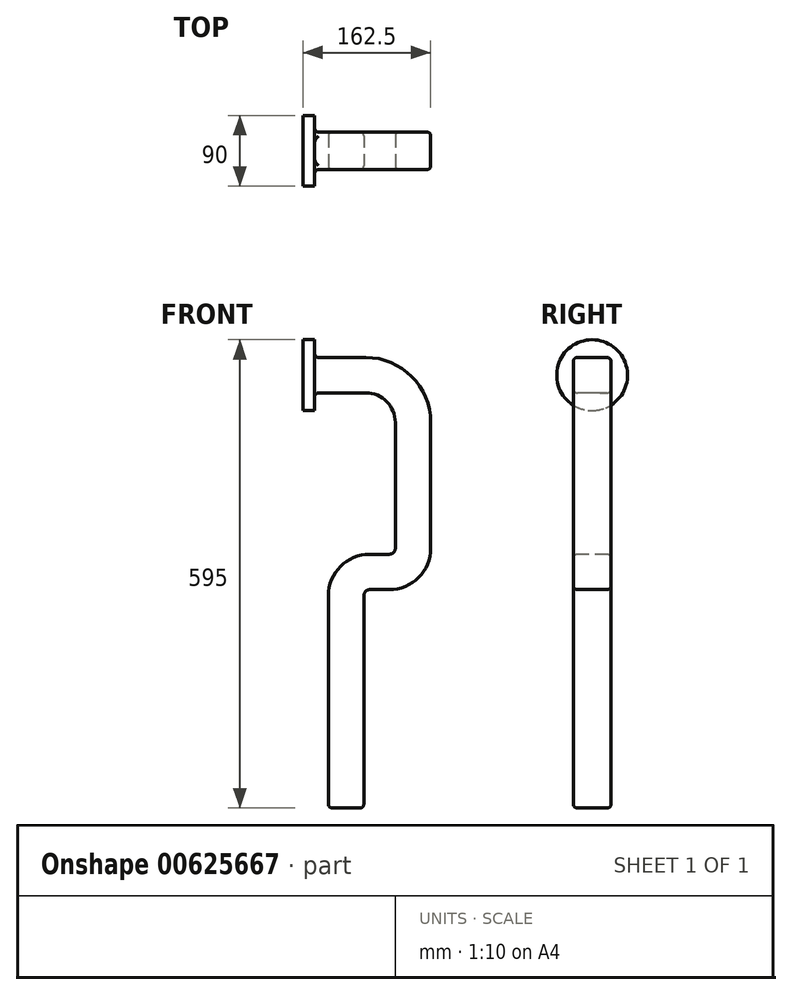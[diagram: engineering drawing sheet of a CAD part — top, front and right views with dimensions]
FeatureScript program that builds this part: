
annotation { "Feature Type Name" : "Feature", "Feature Type Description" : "" }
export const myFeature = defineFeature(function(context is Context, id is Id, definition is map)
    precondition{}
    {
        {
            var Q0;
            Q0=qCreatedBy(makeId("Right.planeOp"),FACE);
            var sketch = newSketch(context, id + "F0", { "sketchPlane" : qUnion([Q0])});
            skCircle(sketch, "E0", {"center": v(0, 0) * mm, "radius": 45 * mm});
            skSolve(sketch);
        }
        {
            var Q0;
            Q0=makeQuery(id+"F0.imprint","IMPRINT",FACE,{"disambiguationData":[TD([[makeQuery(id+"F0.imprint","IMPRINT",EDGE,{"derivedFrom":sQuery(id+"F0.wireOp",EDGE,"E0")}),1.0]])]});
            var Q1;
            Q1=sQuery(id+"F0.wireOp",EDGE,"E0");
            extrude(context, id + "F1", {"entities" : qUnion([Q0]), "surfaceEntities" : qUnion([Q1]), "depth" : 15 * mm, "offsetDistance" : 25 * mm});
        }
        {
            var Q0;
            Q0=makeQuery(id+"F1.opExtrude","CAP_FACE",FACE,{"disambiguationData":[OSD([sQuery(id+"F0.wireOp",EDGE,"E0")])],"isStart":false});
            var sketch = newSketch(context, id + "F2", { "sketchPlane" : qUnion([Q0])});
            skLineSegment(sketch, "E1.bottom", {"start": v(23.85, -22.5) * mm, "end": v(-23.85, -22.5) * mm});
            skLineSegment(sketch, "E1.top", {"start": v(23.85, 22.5) * mm, "end": v(-23.85, 22.5) * mm});
            skLineSegment(sketch, "E1.left", {"start": v(23.85, -22.5) * mm, "end": v(23.85, 22.5) * mm});
            skLineSegment(sketch, "E1.right", {"start": v(-23.85, -22.5) * mm, "end": v(-23.85, 22.5) * mm});
            skPoint(sketch, "E1.middle", {"position": v(0, 0) * mm});
            skSolve(sketch);
        }
        {
            var Q0;
            Q0=qCreatedBy(makeId("Front.planeOp"),FACE);
            var sketch = newSketch(context, id + "F3", { "sketchPlane" : qUnion([Q0])});
            skLineSegment(sketch, "E2", {"start": v(15, 0) * mm, "end": v(80, 0) * mm});
            skLineSegment(sketch, "E3", {"start": v(140, -60) * mm, "end": v(140, -220) * mm});
            skLineSegment(sketch, "E4", {"start": v(110, -250) * mm, "end": v(85, -250) * mm});
            skLineSegment(sketch, "E5", {"start": v(55, -280) * mm, "end": v(55, -550) * mm});
            skPoint(sketch, "E6.visualSharp", {"position": v(140, 0) * mm});
            skArc(sketch, "E6.filletArc", {"start": v(140, -60) * mm, "mid": v(122.43, -17.57) * mm, "end": v(80, 0) * mm});
            skPoint(sketch, "E7.visualSharp", {"position": v(140, -250) * mm});
            skArc(sketch, "E7.filletArc", {"start": v(110, -250) * mm, "mid": v(131.21, -241.21) * mm, "end": v(140, -220) * mm});
            skPoint(sketch, "E8.visualSharp", {"position": v(55, -250) * mm});
            skArc(sketch, "E8.filletArc", {"start": v(85, -250) * mm, "mid": v(63.79, -258.79) * mm, "end": v(55, -280) * mm});
            skSolve(sketch);
        }
        {
            var Q0;
            Q0=makeQuery(id+"F2.imprint","IMPRINT",FACE,{"disambiguationData":[TD([[makeQuery(id+"F2.imprint","IMPRINT",EDGE,{"derivedFrom":sQuery(id+"F2.wireOp",EDGE,"E1.bottom")}),-1.0]])]});
            var Q1;
            Q1=sQuery(id+"F3.wireOp",EDGE,"E2");
            var Q2;
            Q2=sQuery(id+"F3.wireOp",EDGE,"E6.filletArc");
            var Q3;
            Q3=sQuery(id+"F3.wireOp",EDGE,"E3");
            var Q4;
            Q4=sQuery(id+"F3.wireOp",EDGE,"E7.filletArc");
            var Q5;
            Q5=sQuery(id+"F3.wireOp",EDGE,"E4");
            var Q6;
            Q6=sQuery(id+"F3.wireOp",EDGE,"E8.filletArc");
            var Q7;
            Q7=sQuery(id+"F3.wireOp",EDGE,"E5");
            sweep(context, id + "F4", {"operationType" : NewBodyOperationType.ADD, "profiles" : qUnion([Q0]), "path" : qUnion([Q1, Q2, Q3, Q4, Q5, Q6, Q7])});
        }
        {
            var Q0;
            Q0=makeQuery(id+"F4.opSweep","SWEPT_FACE",FACE,{"disambiguationData":[OSD([sQuery(id+"F2.wireOp",EDGE,"E1.right"),sQuery(id+"F3.wireOp",EDGE,"E2")])]});
            var Q1;
            Q1=makeQuery(id+"F4.opSweep","SWEPT_FACE",FACE,{"disambiguationData":[OSD([sQuery(id+"F2.wireOp",EDGE,"E1.left"),sQuery(id+"F3.wireOp",EDGE,"E2")])]});
            var Q2;
            Q2=makeQuery(id+"F4.opSweep","CAP_FACE",FACE,{"disambiguationData":[OSD([sQuery(id+"F2.wireOp",EDGE,"E1.bottom"),sQuery(id+"F2.wireOp",EDGE,"E1.top"),sQuery(id+"F2.wireOp",EDGE,"E1.left"),sQuery(id+"F2.wireOp",EDGE,"E1.right"),sQuery(id+"F3.wireOp",VERTEX,"E5.end")])],"isStart":false});
            fillet(context, id + "F5", {"entities" : qUnion([Q0, Q1, Q2]), "radius" : 5 * mm, "tangentPropagation" : true, "allowEdgeOverflow" : false});
        }
    });
